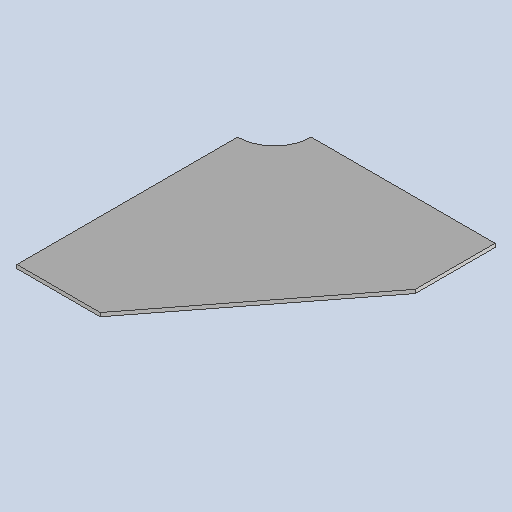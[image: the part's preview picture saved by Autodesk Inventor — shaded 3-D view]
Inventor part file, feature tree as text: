
AUTODESK INVENTOR PART (.ipt)
format: ipt  version: 2025 (Build 290162010, 162A)  size: 185,856 bytes
history: native  units: mm
features: other x5, sketch x2, sheet_metal_op x1
ambient origin geometry x8: Origin, YZ Plane, XZ Plane, XY Plane, X Axis, Y Axis, Z Axis, Center Point
bodies: Solid1 (feature_tree)
feature tree (8):
  other  "TRM 034 motor pillar"
  sheet_metal_op  "Face1"
  other  "Mark1"
  other  "A-Side Definition"
  sketch  "Sketch1"  dims[d0=120.0mm]
  other  "Plate1"
  sketch  "Sketch2"  dims[d1=140.0mm d2=2.0mm d6=200.0mm d9=20.0mm d10=20.0mm d11=20.0mm d16=40.0mm]
  other  "Definition1"
